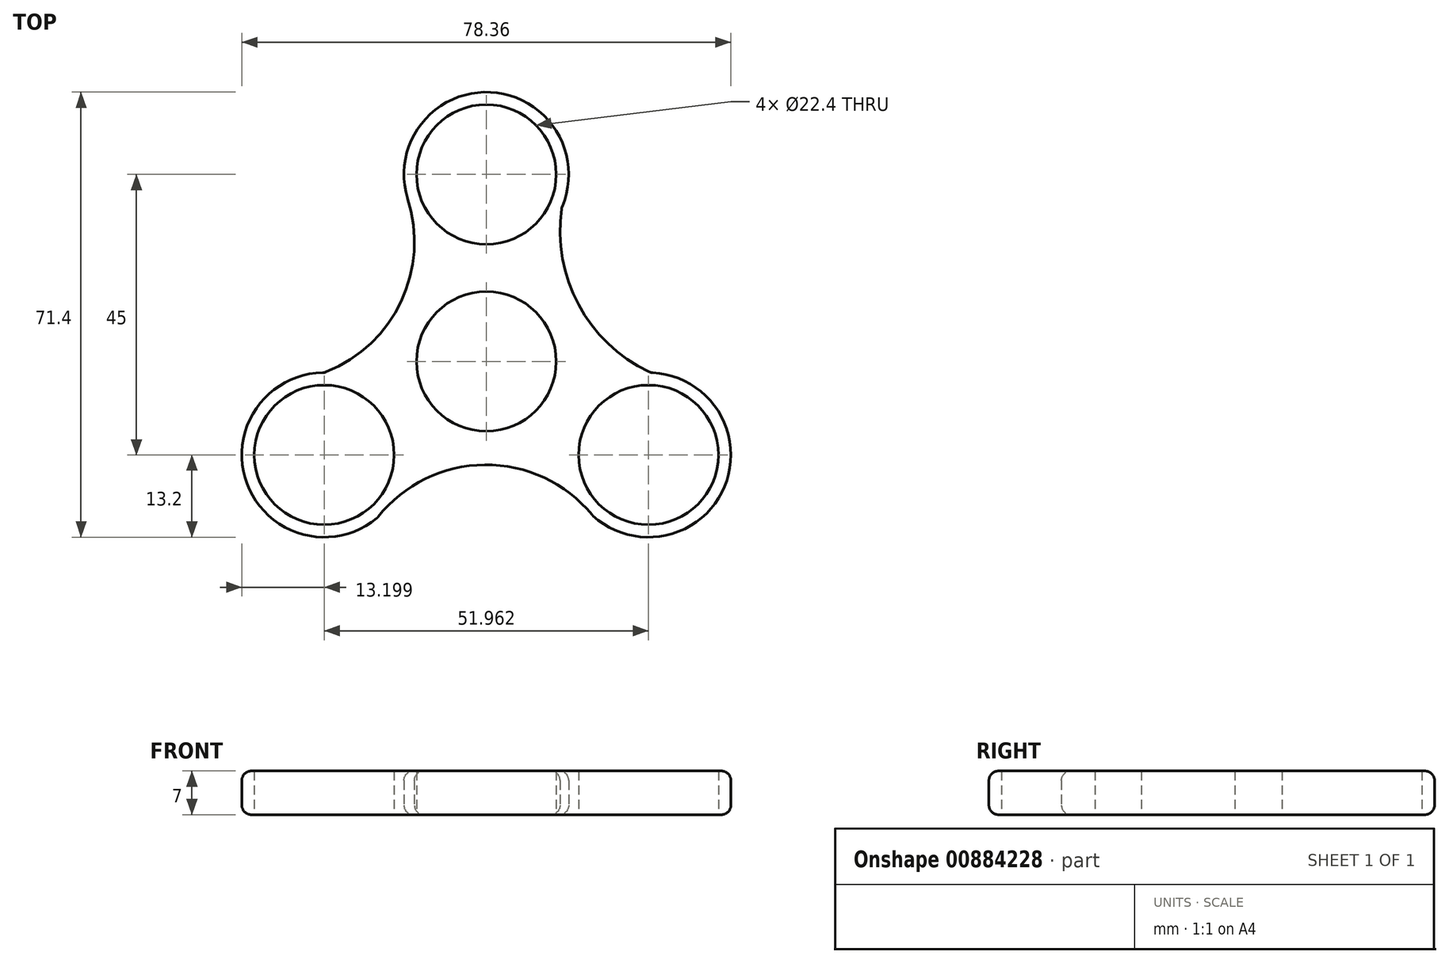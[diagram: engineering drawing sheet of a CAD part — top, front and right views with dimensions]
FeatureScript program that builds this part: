
annotation { "Feature Type Name" : "Feature", "Feature Type Description" : "" }
export const myFeature = defineFeature(function(context is Context, id is Id, definition is map)
    precondition{}
    {
        {
            var Q0;
            Q0=qCreatedBy(makeId("Top.planeOp"),FACE);
            var sketch = newSketch(context, id + "F0", { "sketchPlane" : qUnion([Q0])});
            skCircle(sketch, "E0", {"center": v(0, 0) * mm, "radius": 11.2 * mm});
            skCircle(sketch, "E1", {"center": v(0, 30) * mm, "radius": 11.2 * mm});
            skArc(sketch, "E2", {"start": v(12.1, 24.72) * mm, "mid": v(0.6, 43.19) * mm, "end": v(-12.53, 25.85) * mm});
            skArc(sketch, "E3.1.0", {"start": v(-25.96, -1.8) * mm, "mid": v(-37.7, -21.08) * mm, "end": v(-15.17, -22.58) * mm});
            skArc(sketch, "E3.2.0", {"start": v(15.47, -22.98) * mm, "mid": v(37.72, -21.04) * mm, "end": v(26.36, -1.8) * mm});
            skLineSegment(sketch, "E4", {"start": v(0, 30) * mm, "end": v(25.98, -15) * mm, "construction": true});
            skLineSegment(sketch, "E5", {"start": v(-25.98, -15) * mm, "end": v(0, 0) * mm, "construction": true});
            skLineSegment(sketch, "E6", {"start": v(0, 0) * mm, "end": v(38.9, 30) * mm, "construction": true});
            skLineSegment(sketch, "E7", {"start": v(38.9, 30) * mm, "end": v(48.85, 12.75) * mm, "construction": true});
            skArc(sketch, "E8", {"start": v(-25.96, -1.8) * mm, "mid": v(-13.72, 9.52) * mm, "end": v(-12.63, 26.17) * mm});
            skArc(sketch, "E9", {"start": v(12.1, 24.72) * mm, "mid": v(14.8, 9.07) * mm, "end": v(26.36, -1.8) * mm});
            skArc(sketch, "E10", {"start": v(17.01, -24.69) * mm, "mid": v(-0.3, -16.58) * mm, "end": v(-17.43, -25.06) * mm});
            skCircle(sketch, "E11", {"center": v(25.98, -15) * mm, "radius": 11.2 * mm});
            skCircle(sketch, "E12", {"center": v(-25.98, -15) * mm, "radius": 11.2 * mm});
            skSolve(sketch);
        }
        {
            var Q0;
            Q0=makeQuery(id+"F0.imprint","IMPRINT",FACE,{"disambiguationData":[TD([[makeQuery(id+"F0.imprint","IMPRINT",EDGE,{"derivedFrom":sQuery(id+"F0.wireOp",EDGE,"E0")}),-1.0]])]});
            extrude(context, id + "F1", {"entities" : qUnion([Q0]), "depth" : 7 * mm, "offsetDistance" : 25 * mm});
        }
        {
            var Q0;
            Q0=makeQuery(id+"F1.opExtrude","SWEPT_FACE",FACE,{"disambiguationData":[OSD([sQuery(id+"F0.wireOp",EDGE,"E3.1.0")])]});
            var Q1;
            Q1=makeQuery(id+"F1.opExtrude","SWEPT_FACE",FACE,{"disambiguationData":[OSD([sQuery(id+"F0.wireOp",EDGE,"E10")])]});
            var Q2;
            Q2=makeQuery(id+"F1.opExtrude","SWEPT_FACE",FACE,{"disambiguationData":[OSD([sQuery(id+"F0.wireOp",EDGE,"E3.2.0")])]});
            var Q3;
            Q3=makeQuery(id+"F1.opExtrude","SWEPT_FACE",FACE,{"disambiguationData":[OSD([sQuery(id+"F0.wireOp",EDGE,"E9")])]});
            var Q4;
            Q4=makeQuery(id+"F1.opExtrude","SWEPT_FACE",FACE,{"disambiguationData":[OSD([sQuery(id+"F0.wireOp",EDGE,"E2")])]});
            var Q5;
            Q5=makeQuery(id+"F1.opExtrude","SWEPT_FACE",FACE,{"disambiguationData":[OSD([sQuery(id+"F0.wireOp",EDGE,"E8")])]});
            fillet(context, id + "F2", {"entities" : qUnion([Q0, Q1, Q2, Q3, Q4, Q5]), "radius" : 1.5 * mm, "tangentPropagation" : true, "allowEdgeOverflow" : false});
        }
    });
